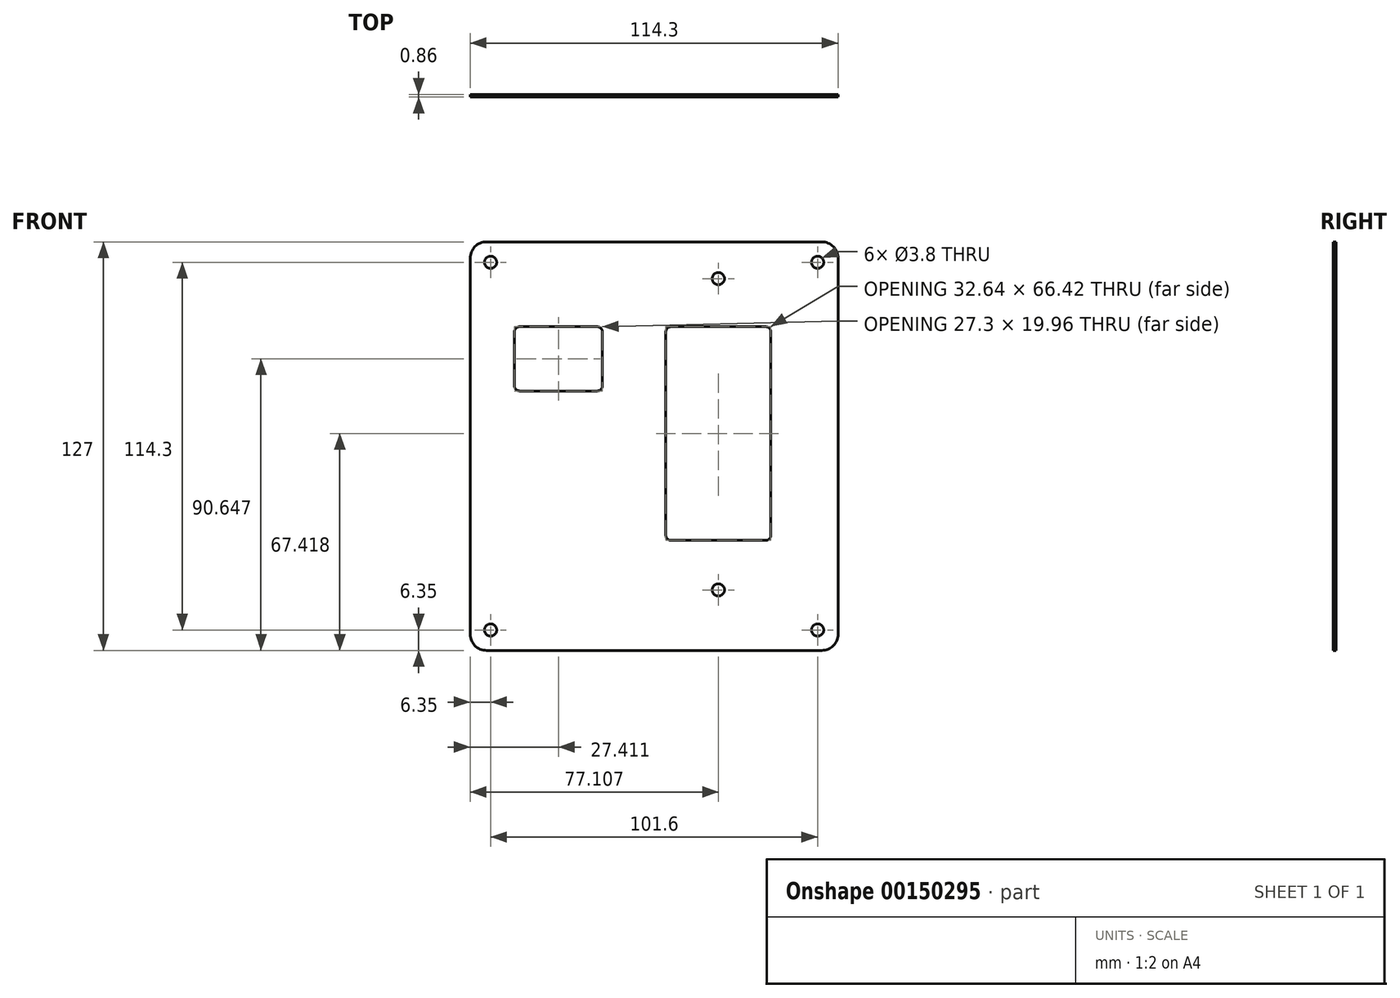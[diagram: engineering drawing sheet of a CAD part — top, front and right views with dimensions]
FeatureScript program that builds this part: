
annotation { "Feature Type Name" : "Feature", "Feature Type Description" : "" }
export const myFeature = defineFeature(function(context is Context, id is Id, definition is map)
    precondition{}
    {
        {
            var Q0;
            Q0=qCreatedBy(makeId("Front.planeOp"),FACE);
            var sketch = newSketch(context, id + "F0", { "sketchPlane" : qUnion([Q0])});
            skLineSegment(sketch, "E0.bottom", {"start": v(57.15, 63.5) * mm, "end": v(-57.15, 63.5) * mm});
            skLineSegment(sketch, "E0.top", {"start": v(57.15, -63.5) * mm, "end": v(-57.15, -63.5) * mm});
            skLineSegment(sketch, "E0.left", {"start": v(57.15, 63.5) * mm, "end": v(57.15, -63.5) * mm});
            skLineSegment(sketch, "E0.right", {"start": v(-57.15, 63.5) * mm, "end": v(-57.15, -63.5) * mm});
            skPoint(sketch, "E0.middle", {"position": v(0, 0) * mm});
            skSolve(sketch);
        }
        {
            var Q0;
            Q0=makeQuery(id+"F0.imprint","IMPRINT",FACE,{"disambiguationData":[TD([[makeQuery(id+"F0.imprint","IMPRINT",EDGE,{"derivedFrom":sQuery(id+"F0.wireOp",EDGE,"E0.bottom")}),1.0]])]});
            extrude(context, id + "F1", {"entities" : qUnion([Q0]), "oppositeDirection" : true, "depth" : 0.86 * mm});
        }
        {
            var Q0;
            Q0=makeQuery(id+"F1.opExtrude","CAP_FACE",FACE,{"disambiguationData":[OSD([sQuery(id+"F0.wireOp",EDGE,"E0.bottom"),sQuery(id+"F0.wireOp",EDGE,"E0.top"),sQuery(id+"F0.wireOp",EDGE,"E0.left"),sQuery(id+"F0.wireOp",EDGE,"E0.right")])],"isStart":true});
            var sketch = newSketch(context, id + "F2", { "sketchPlane" : qUnion([Q0])});
            skLineSegment(sketch, "E1.bottom", {"start": v(-17.67, 37.13) * mm, "end": v(-41.8, 37.13) * mm});
            skLineSegment(sketch, "E1.top", {"start": v(-17.67, 17.16) * mm, "end": v(-41.8, 17.16) * mm});
            skLineSegment(sketch, "E1.left", {"start": v(-16.09, 35.54) * mm, "end": v(-16.09, 18.75) * mm});
            skLineSegment(sketch, "E1.right", {"start": v(-43.4, 35.54) * mm, "end": v(-43.4, 18.75) * mm});
            skPoint(sketch, "E1.middle", {"position": v(-29.74, 27.15) * mm});
            skLineSegment(sketch, "E2.bottom", {"start": v(34.69, 37.13) * mm, "end": v(5.22, 37.13) * mm});
            skLineSegment(sketch, "E2.top", {"start": v(34.69, -29.3) * mm, "end": v(5.22, -29.3) * mm});
            skLineSegment(sketch, "E2.left", {"start": v(36.28, 35.54) * mm, "end": v(36.28, -27.7) * mm});
            skLineSegment(sketch, "E2.right", {"start": v(3.64, 35.54) * mm, "end": v(3.64, -27.7) * mm});
            skPoint(sketch, "E2.middle", {"position": v(19.96, 3.92) * mm});
            skPoint(sketch, "E3.visualSharp", {"position": v(-43.4, 37.13) * mm});
            skArc(sketch, "E3.filletArc", {"start": v(-41.8, 37.13) * mm, "mid": v(-42.93, 36.66) * mm, "end": v(-43.4, 35.54) * mm});
            skPoint(sketch, "E4.visualSharp", {"position": v(-16.09, 37.13) * mm});
            skArc(sketch, "E4.filletArc", {"start": v(-16.09, 35.54) * mm, "mid": v(-16.55, 36.66) * mm, "end": v(-17.67, 37.13) * mm});
            skPoint(sketch, "E5.visualSharp", {"position": v(-16.09, 17.16) * mm});
            skArc(sketch, "E5.filletArc", {"start": v(-17.67, 17.16) * mm, "mid": v(-16.55, 17.63) * mm, "end": v(-16.09, 18.75) * mm});
            skPoint(sketch, "E6.visualSharp", {"position": v(-43.4, 17.16) * mm});
            skArc(sketch, "E6.filletArc", {"start": v(-43.4, 18.75) * mm, "mid": v(-42.93, 17.63) * mm, "end": v(-41.8, 17.16) * mm});
            skPoint(sketch, "E7.visualSharp", {"position": v(3.64, 37.13) * mm});
            skArc(sketch, "E7.filletArc", {"start": v(5.22, 37.13) * mm, "mid": v(4.1, 36.66) * mm, "end": v(3.64, 35.54) * mm});
            skPoint(sketch, "E8.visualSharp", {"position": v(36.28, 37.13) * mm});
            skArc(sketch, "E8.filletArc", {"start": v(36.28, 35.54) * mm, "mid": v(35.81, 36.66) * mm, "end": v(34.69, 37.13) * mm});
            skPoint(sketch, "E9.visualSharp", {"position": v(36.28, -29.3) * mm});
            skArc(sketch, "E9.filletArc", {"start": v(34.69, -29.3) * mm, "mid": v(35.81, -28.83) * mm, "end": v(36.28, -27.7) * mm});
            skPoint(sketch, "E10.visualSharp", {"position": v(3.64, -29.3) * mm});
            skArc(sketch, "E10.filletArc", {"start": v(3.64, -27.7) * mm, "mid": v(4.1, -28.83) * mm, "end": v(5.22, -29.3) * mm});
            skSolve(sketch);
        }
        {
            var Q0;
            Q0 = qSketchRegion(id + "F2", true);
            extrude(context, id + "F3", {"entities" : qUnion([Q0]), "operationType" : NewBodyOperationType.REMOVE, "endBound" : BoundingType.UP_TO_NEXT, "oppositeDirection" : true, "depth" : 25.4 * mm});
        }
        {
            var Q0;
            Q0=makeQuery(id+"F1.opExtrude","SWEPT_EDGE",EDGE,{"disambiguationData":[OSD([sQuery(id+"F0.wireOp",EDGE,"E0.bottom"),sQuery(id+"F0.wireOp",EDGE,"E0.right")])]});
            var Q1;
            Q1=makeQuery(id+"F1.opExtrude","SWEPT_EDGE",EDGE,{"disambiguationData":[OSD([sQuery(id+"F0.wireOp",EDGE,"E0.bottom"),sQuery(id+"F0.wireOp",EDGE,"E0.left")])]});
            var Q2;
            Q2=makeQuery(id+"F1.opExtrude","SWEPT_EDGE",EDGE,{"disambiguationData":[OSD([sQuery(id+"F0.wireOp",EDGE,"E0.top"),sQuery(id+"F0.wireOp",EDGE,"E0.left")])]});
            var Q3;
            Q3=makeQuery(id+"F1.opExtrude","SWEPT_EDGE",EDGE,{"disambiguationData":[OSD([sQuery(id+"F0.wireOp",EDGE,"E0.top"),sQuery(id+"F0.wireOp",EDGE,"E0.right")])]});
            fillet(context, id + "F4", {"entities" : qUnion([Q0, Q1, Q2, Q3]), "radius" : 5.08 * mm, "tangentPropagation" : true, "allowEdgeOverflow" : false});
        }
        {
            var Q0;
            Q0=makeQuery(id+"F1.opExtrude","CAP_FACE",FACE,{"disambiguationData":[OSD([sQuery(id+"F0.wireOp",EDGE,"E0.bottom"),sQuery(id+"F0.wireOp",EDGE,"E0.top"),sQuery(id+"F0.wireOp",EDGE,"E0.left"),sQuery(id+"F0.wireOp",EDGE,"E0.right")])],"isStart":true});
            var sketch = newSketch(context, id + "F5", { "sketchPlane" : qUnion([Q0])});
            skCircle(sketch, "E11", {"center": v(19.96, 52.06) * mm, "radius": 1.44 * mm});
            skCircle(sketch, "E12", {"center": v(19.96, -44.68) * mm, "radius": 1.44 * mm});
            skPoint(sketch, "E13", {"position": v(19.96, -29.3) * mm});
            skSolve(sketch);
        }
        {
            var Q0;
            Q0=sQuery(id+"F5.wireOp",VERTEX,"E11.center");
            var Q1;
            Q1=sQuery(id+"F5.wireOp",VERTEX,"E12.center");
            var Q2;
            Q2=makeQuery(id+"F1.opExtrude","SWEPT_BODY",BODY,{"disambiguationData":[OSD([sQuery(id+"F0.wireOp",EDGE,"E0.bottom"),sQuery(id+"F0.wireOp",EDGE,"E0.top"),sQuery(id+"F0.wireOp",EDGE,"E0.left"),sQuery(id+"F0.wireOp",EDGE,"E0.right")])]});
            hole(context, id + "F6", {"style" : HoleStyle.SIMPLE, "endStyle" : HoleEndStyle.THROUGH, "standardTappedOrClearance" : lookupTablePath({ "standard" : "ANSI", "fit" : "Normal (ASME)", "size" : "#6", "type" : "Clearance" }), "standardBlindInLast" : lookupTablePath({ "fit" : "Free", "standard" : "ANSI", "size" : "#6", "type" : "Clearance" }), "holeDiameter" : 3.8 * mm, "locations" : qUnion([Q0, Q1]), "scope" : qUnion([Q2]), "isTappedThrough" : true});
        }
        {
            var Q0;
            Q0=makeQuery(id+"F1.opExtrude","CAP_FACE",FACE,{"disambiguationData":[OSD([sQuery(id+"F0.wireOp",EDGE,"E0.bottom"),sQuery(id+"F0.wireOp",EDGE,"E0.top"),sQuery(id+"F0.wireOp",EDGE,"E0.left"),sQuery(id+"F0.wireOp",EDGE,"E0.right")])],"isStart":true});
            var sketch = newSketch(context, id + "F7", { "sketchPlane" : qUnion([Q0])});
            skPoint(sketch, "E14", {"position": v(-50.8, 57.15) * mm});
            skPoint(sketch, "E15", {"position": v(50.8, 57.15) * mm});
            skPoint(sketch, "E16", {"position": v(50.8, -57.15) * mm});
            skPoint(sketch, "E17", {"position": v(-50.8, -57.15) * mm});
            skSolve(sketch);
        }
        {
            var Q0;
            Q0=sQuery(id+"F7.wireOp",VERTEX,"E14");
            var Q1;
            Q1=sQuery(id+"F7.wireOp",VERTEX,"E15");
            var Q2;
            Q2=sQuery(id+"F7.wireOp",VERTEX,"E16");
            var Q3;
            Q3=sQuery(id+"F7.wireOp",VERTEX,"E17");
            var Q4;
            Q4=makeQuery(id+"F1.opExtrude","SWEPT_BODY",BODY,{"disambiguationData":[OSD([sQuery(id+"F0.wireOp",EDGE,"E0.bottom"),sQuery(id+"F0.wireOp",EDGE,"E0.top"),sQuery(id+"F0.wireOp",EDGE,"E0.left"),sQuery(id+"F0.wireOp",EDGE,"E0.right")])]});
            hole(context, id + "F8", {"style" : HoleStyle.SIMPLE, "endStyle" : HoleEndStyle.THROUGH, "standardTappedOrClearance" : lookupTablePath({ "standard" : "ANSI", "fit" : "Normal (ASME)", "size" : "#6", "type" : "Clearance" }), "standardBlindInLast" : lookupTablePath({ "fit" : "Free", "standard" : "ANSI", "size" : "#6", "type" : "Clearance" }), "holeDiameter" : 3.8 * mm, "locations" : qUnion([Q0, Q1, Q2, Q3]), "scope" : qUnion([Q4]), "isTappedThrough" : true});
        }
    });
